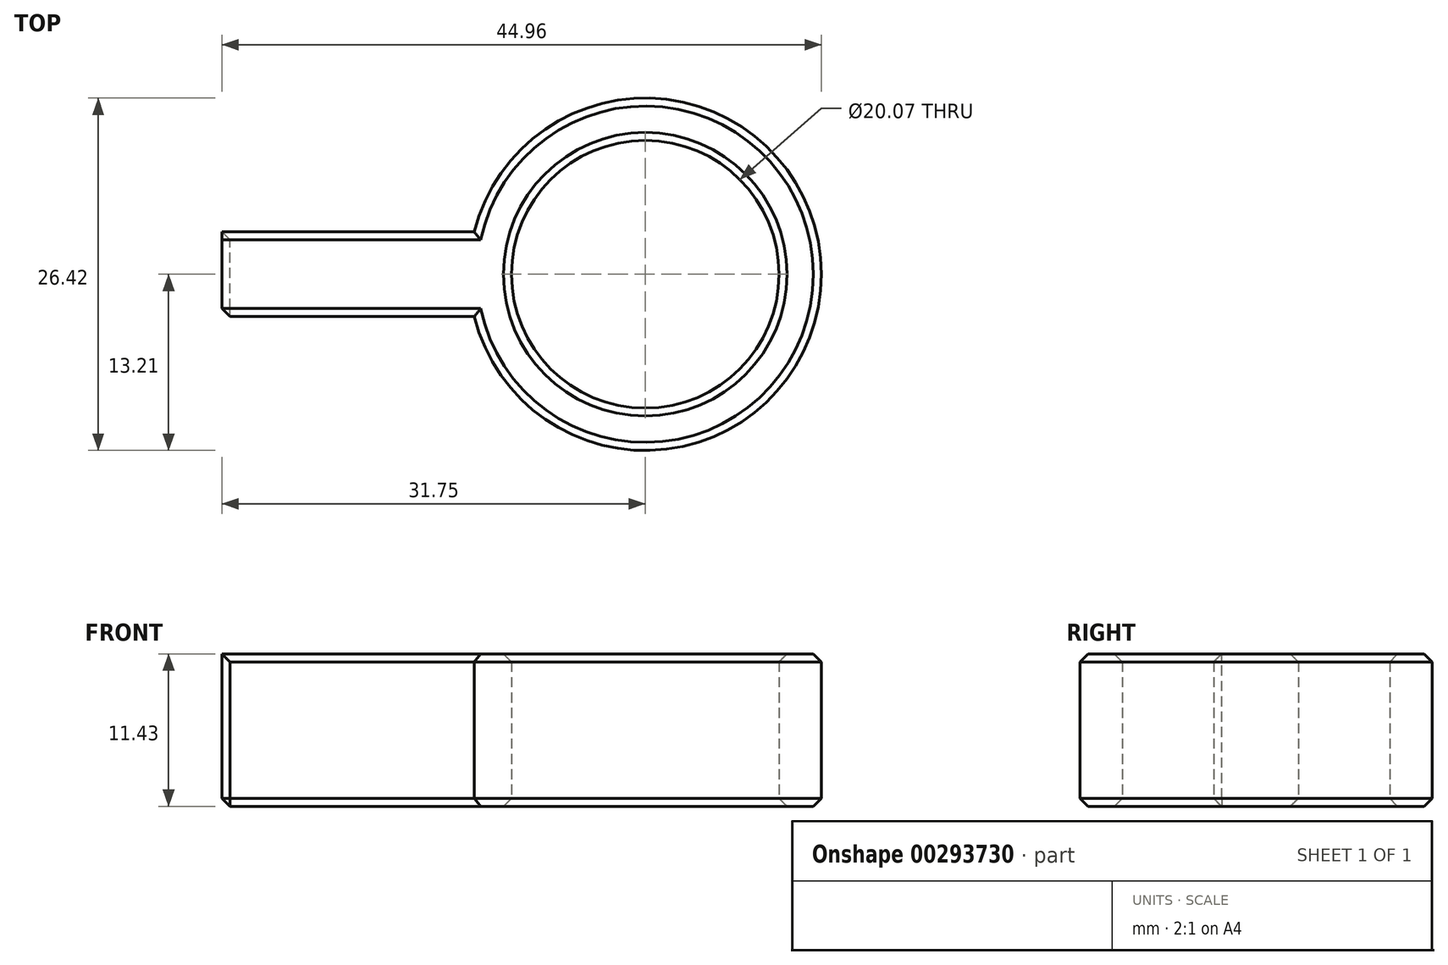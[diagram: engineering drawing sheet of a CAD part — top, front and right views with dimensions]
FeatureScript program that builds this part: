
annotation { "Feature Type Name" : "Feature", "Feature Type Description" : "" }
export const myFeature = defineFeature(function(context is Context, id is Id, definition is map)
    precondition{}
    {
        {
            var Q0;
            Q0=qCreatedBy(makeId("Top.planeOp"),FACE);
            var sketch = newSketch(context, id + "F0", { "sketchPlane" : qUnion([Q0])});
            skArc(sketch, "E0", {"start": v(-12.82, -3.17) * mm, "mid": v(13.2, 0) * mm, "end": v(-12.82, 3.18) * mm});
            skLineSegment(sketch, "E1.bottom", {"start": v(-31.75, -3.17) * mm, "end": v(-12.82, -3.17) * mm});
            skLineSegment(sketch, "E1.top", {"start": v(-31.75, 3.18) * mm, "end": v(-12.82, 3.18) * mm});
            skLineSegment(sketch, "E1.left", {"start": v(-31.75, -3.17) * mm, "end": v(-31.75, 3.17) * mm});
            skCircle(sketch, "E2", {"center": v(0, 0) * mm, "radius": 10.03 * mm});
            skSolve(sketch);
        }
        {
            var Q0;
            Q0 = qSketchRegion(id + "F0", true);
            extrude(context, id + "F1", {"entities" : qUnion([Q0]), "depth" : 11.43 * mm});
        }
        {
            var Q0;
            Q0=makeQuery(id+"F1.opExtrude","CAP_EDGE",EDGE,{"disambiguationData":[OSD([sQuery(id+"F0.wireOp",EDGE,"E2")])],"isStart":false});
            var Q1;
            Q1=makeQuery(id+"F1.opExtrude","CAP_EDGE",EDGE,{"disambiguationData":[OSD([sQuery(id+"F0.wireOp",EDGE,"E0")])],"isStart":false});
            var Q2;
            Q2=makeQuery(id+"F1.opExtrude","CAP_EDGE",EDGE,{"disambiguationData":[OSD([sQuery(id+"F0.wireOp",EDGE,"E1.bottom")])],"isStart":false});
            var Q3;
            Q3=makeQuery(id+"F1.opExtrude","CAP_EDGE",EDGE,{"disambiguationData":[OSD([sQuery(id+"F0.wireOp",EDGE,"E1.top")])],"isStart":false});
            var Q4;
            Q4=makeQuery(id+"F1.opExtrude","CAP_EDGE",EDGE,{"disambiguationData":[OSD([sQuery(id+"F0.wireOp",EDGE,"E1.bottom")])],"isStart":true});
            var Q5;
            Q5=makeQuery(id+"F1.opExtrude","SWEPT_EDGE",EDGE,{"disambiguationData":[OSD([sQuery(id+"F0.wireOp",EDGE,"E1.bottom"),sQuery(id+"F0.wireOp",EDGE,"E1.left")])]});
            var Q6;
            Q6=makeQuery(id+"F1.opExtrude","CAP_EDGE",EDGE,{"disambiguationData":[OSD([sQuery(id+"F0.wireOp",EDGE,"E0")])],"isStart":true});
            var Q7;
            Q7=makeQuery(id+"F1.opExtrude","CAP_EDGE",EDGE,{"disambiguationData":[OSD([sQuery(id+"F0.wireOp",EDGE,"E2")])],"isStart":true});
            var Q8;
            Q8=makeQuery(id+"F1.opExtrude","CAP_EDGE",EDGE,{"disambiguationData":[OSD([sQuery(id+"F0.wireOp",EDGE,"E1.top")])],"isStart":true});
            var Q9;
            Q9=makeQuery(id+"F1.opExtrude","CAP_EDGE",EDGE,{"disambiguationData":[OSD([sQuery(id+"F0.wireOp",EDGE,"E1.left")])],"isStart":true});
            chamfer(context, id + "F2", {"entities" : qUnion([Q0, Q1, Q2, Q3, Q4, Q5, Q6, Q7, Q8, Q9]), "width" : .6 * mm, "tangentPropagation" : true});
        }
    });
